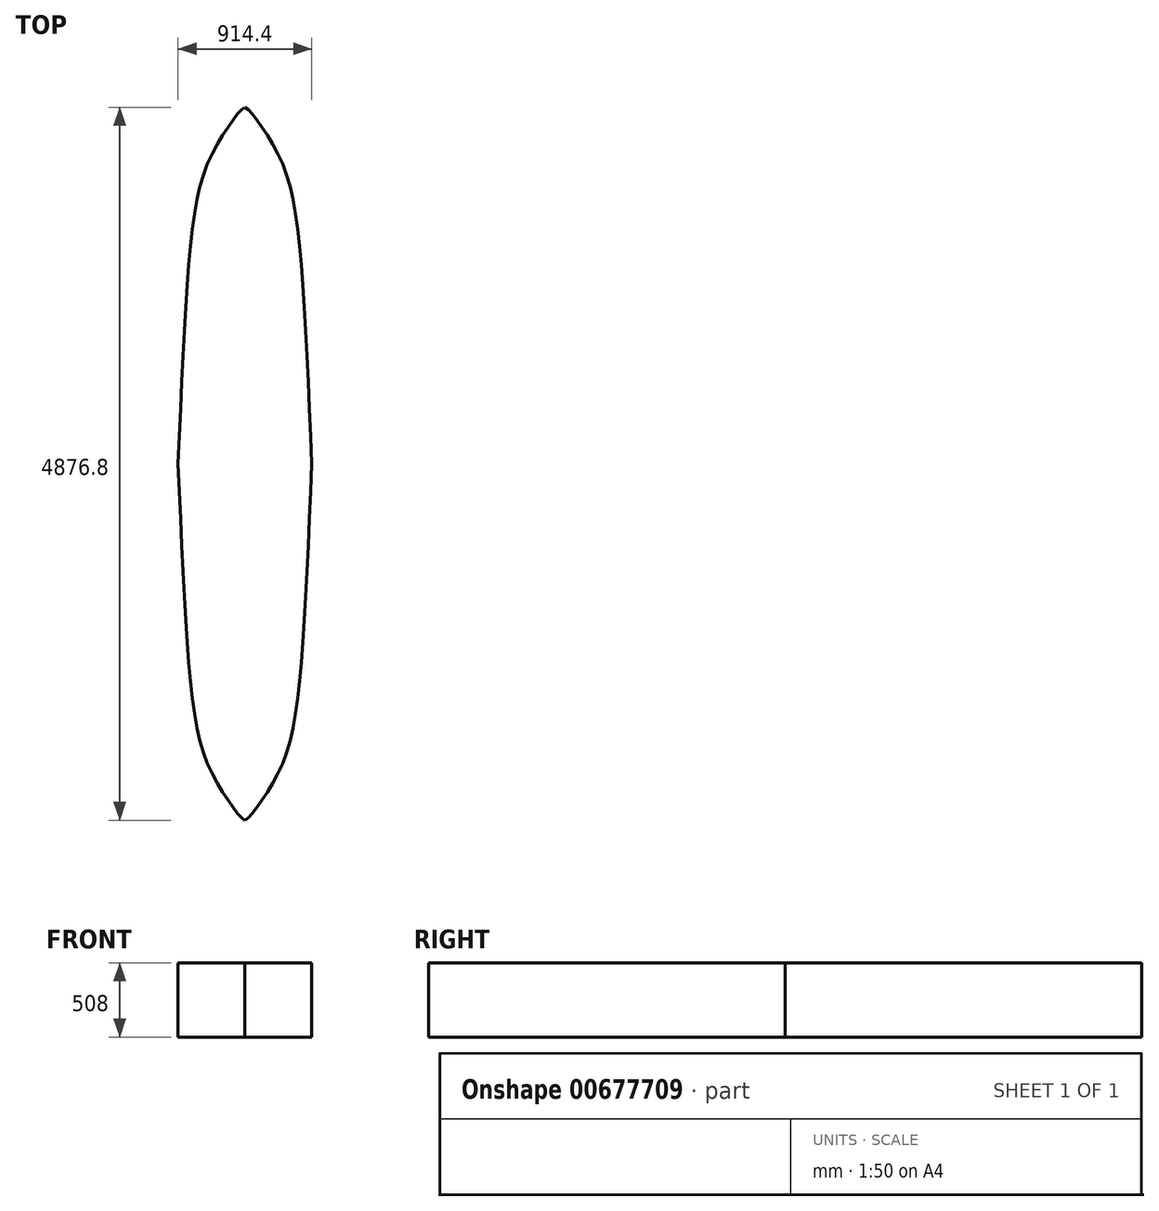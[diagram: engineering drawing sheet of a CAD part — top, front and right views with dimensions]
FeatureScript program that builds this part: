
annotation { "Feature Type Name" : "Feature", "Feature Type Description" : "" }
export const myFeature = defineFeature(function(context is Context, id is Id, definition is map)
    precondition{}
    {
        {
            var Q0;
            Q0=qCreatedBy(makeId("Top.planeOp"),FACE);
            var sketch = newSketch(context, id + "F0", { "sketchPlane" : qUnion([Q0])});
            skFitSpline(sketch, "E0", {"points": [v(45.85, 6631.91) * mm, v(73, 6610.83) * mm, v(125.74, 6546.63) * mm, v(212.49, 6418.13) * mm, v(310.65, 6224.53) * mm, v(384.28, 5946.4) * mm, v(444.27, 5376.48) * mm, v(503.05, 4193.51) * mm], "startDerivative": vector(521.99, -352.45) * mm, "endDerivative": vector(185.12, -4352.52) * mm});
            skFitSpline(sketch, "E1.MirrorCS", {"points": [v(45.85, 6631.91) * mm, v(18.7, 6610.83) * mm, v(-34.05, 6546.63) * mm, v(-120.79, 6418.13) * mm, v(-218.95, 6224.53) * mm, v(-292.58, 5946.4) * mm, v(-352.57, 5376.48) * mm, v(-411.35, 4193.51) * mm], "startDerivative": vector(-521.99, -352.45) * mm, "endDerivative": vector(-185.12, -4352.52) * mm});
            skFitSpline(sketch, "E2.MirrorCS", {"points": [v(45.85, 1755.11) * mm, v(18.7, 1776.2) * mm, v(-34.05, 1840.4) * mm, v(-120.79, 1968.9) * mm, v(-218.95, 2162.5) * mm, v(-292.58, 2440.64) * mm, v(-352.57, 3010.55) * mm, v(-411.35, 4193.51) * mm], "startDerivative": vector(-521.99, 352.45) * mm, "endDerivative": vector(-185.12, 4352.52) * mm});
            skFitSpline(sketch, "E3.MirrorCS", {"points": [v(45.85, 1755.11) * mm, v(73, 1776.2) * mm, v(125.74, 1840.4) * mm, v(212.49, 1968.9) * mm, v(310.65, 2162.5) * mm, v(384.28, 2440.64) * mm, v(444.27, 3010.55) * mm, v(503.05, 4193.51) * mm], "startDerivative": vector(521.99, 352.45) * mm, "endDerivative": vector(185.12, 4352.52) * mm});
            skSolve(sketch);
        }
        {
            var Q0;
            Q0 = qSketchRegion(id + "F0", true);
            extrude(context, id + "F1", {"entities" : qUnion([Q0]), "depth" : 508 * mm, "offsetDistance" : 25.4 * mm});
        }
    });
